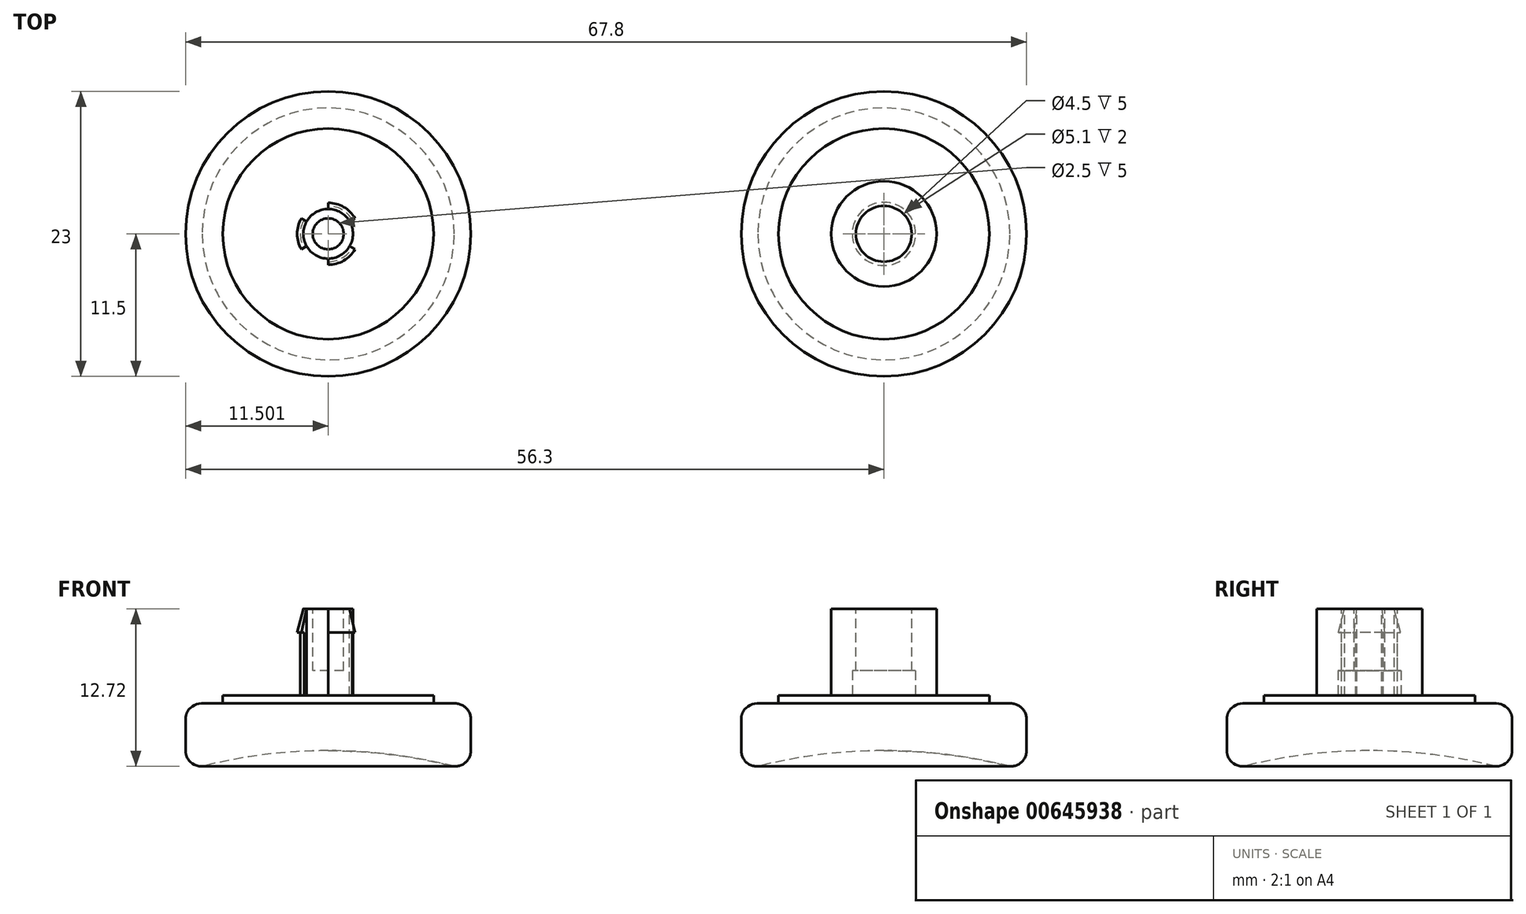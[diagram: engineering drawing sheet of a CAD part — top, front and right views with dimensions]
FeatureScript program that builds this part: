
annotation { "Feature Type Name" : "Feature", "Feature Type Description" : "" }
export const myFeature = defineFeature(function(context is Context, id is Id, definition is map)
    precondition{}
    {
        {
            var Q0;
            Q0=qCreatedBy(makeId("Top.planeOp"),FACE);
            var sketch = newSketch(context, id + "F0", { "sketchPlane" : qUnion([Q0])});
            skCircle(sketch, "E0", {"center": v(0, 0) * mm, "radius": 11.5 * mm});
            skCircle(sketch, "E1", {"center": v(0, 0) * mm, "radius": 4.25 * mm});
            skCircle(sketch, "E2", {"center": v(0, 0) * mm, "radius": 8.5 * mm});
            skSolve(sketch);
        }
        {
            var Q0;
            Q0=makeQuery(id+"F0.imprint","IMPRINT",FACE,{"disambiguationData":[TD([[makeQuery(id+"F0.imprint","IMPRINT",EDGE,{"derivedFrom":sQuery(id+"F0.wireOp",EDGE,"E0")}),1.0]])]});
            extrude(context, id + "F1", {"entities" : qUnion([Q0]), "depth" : 5.08 * mm, "offsetDistance" : 25.4 * mm});
        }
        {
            var Q0;
            Q0=makeQuery(id+"F0.imprint","IMPRINT",FACE,{"disambiguationData":[TD([[makeQuery(id+"F0.imprint","IMPRINT",EDGE,{"derivedFrom":sQuery(id+"F0.wireOp",EDGE,"E1")}),-1.0]])]});
            extrude(context, id + "F2", {"entities" : qUnion([Q0]), "operationType" : NewBodyOperationType.ADD, "depth" : 5.7 * mm, "offsetDistance" : 25.4 * mm});
        }
        {
            var Q0;
            Q0=makeQuery(id+"F0.imprint","IMPRINT",FACE,{"disambiguationData":[TD([[makeQuery(id+"F0.imprint","IMPRINT",EDGE,{"derivedFrom":sQuery(id+"F0.wireOp",EDGE,"E1")}),1.0]])]});
            extrude(context, id + "F3", {"entities" : qUnion([Q0]), "operationType" : NewBodyOperationType.ADD, "depth" : 7 * mm + 5.7 * mm, "offsetDistance" : 25.4 * mm});
        }
        {
            var Q0;
            Q0=makeQuery(id+"F1.opExtrude","CAP_EDGE",EDGE,{"disambiguationData":[OSD([sQuery(id+"F0.wireOp",EDGE,"E0")])],"isStart":false});
            var Q1;
            Q1=makeQuery(id+"F1.opExtrude","CAP_EDGE",EDGE,{"disambiguationData":[OSD([sQuery(id+"F0.wireOp",EDGE,"E0")])],"isStart":true});
            fillet(context, id + "F4", {"entities" : qUnion([Q0, Q1]), "radius" : 1.27 * mm, "tangentPropagation" : true, "allowEdgeOverflow" : false});
        }
        {
            var Q0;
            Q0=qCreatedBy(makeId("Top.planeOp"),FACE);
            var sketch = newSketch(context, id + "F5", { "sketchPlane" : qUnion([Q0])});
            skCircle(sketch, "E3", {"center": v(-44.8, 0) * mm, "radius": 11.5 * mm});
            skCircle(sketch, "E4", {"center": v(-44.8, 0) * mm, "radius": 8.5 * mm});
            skCircle(sketch, "E5", {"center": v(-44.8, 0) * mm, "radius": 2.5 * mm});
            skSolve(sketch);
        }
        {
            var Q0;
            Q0=makeQuery(id+"F5.imprint","IMPRINT",FACE,{"disambiguationData":[TD([[makeQuery(id+"F5.imprint","IMPRINT",EDGE,{"derivedFrom":sQuery(id+"F5.wireOp",EDGE,"E3")}),1.0]])]});
            extrude(context, id + "F6", {"entities" : qUnion([Q0]), "depth" : 5.08 * mm, "offsetDistance" : 25.4 * mm});
        }
        {
            var Q0;
            Q0=makeQuery(id+"F5.imprint","IMPRINT",FACE,{"disambiguationData":[TD([[makeQuery(id+"F5.imprint","IMPRINT",EDGE,{"derivedFrom":sQuery(id+"F5.wireOp",EDGE,"E4")}),1.0]])]});
            extrude(context, id + "F7", {"entities" : qUnion([Q0]), "operationType" : NewBodyOperationType.ADD, "depth" : 5.7 * mm, "offsetDistance" : 25.4 * mm});
        }
        {
            var Q0;
            Q0=makeQuery(id+"F5.imprint","IMPRINT",FACE,{"disambiguationData":[TD([[makeQuery(id+"F5.imprint","IMPRINT",EDGE,{"derivedFrom":sQuery(id+"F5.wireOp",EDGE,"E5")}),1.0]])]});
            extrude(context, id + "F8", {"entities" : qUnion([Q0]), "operationType" : NewBodyOperationType.ADD, "depth" : 7 * mm + 5.7 * mm, "offsetDistance" : 25.4 * mm});
        }
        {
            var Q0;
            Q0=makeQuery(id+"F3.opExtrude","CAP_FACE",FACE,{"disambiguationData":[OSD([sQuery(id+"F0.wireOp",EDGE,"E1")])],"isStart":false});
            var sketch = newSketch(context, id + "F9", { "sketchPlane" : qUnion([Q0])});
            skCircle(sketch, "E6", {"center": v(0, 0) * mm, "radius": 2.25 * mm});
            skSolve(sketch);
        }
        {
            var Q0;
            Q0=makeQuery(id+"F9.imprint","IMPRINT",FACE,{"disambiguationData":[TD([[makeQuery(id+"F9.imprint","IMPRINT",EDGE,{"derivedFrom":sQuery(id+"F9.wireOp",EDGE,"E6")}),1.0]])]});
            extrude(context, id + "F10", {"entities" : qUnion([Q0]), "operationType" : NewBodyOperationType.REMOVE, "oppositeDirection" : true, "depth" : 7 * mm});
        }
        {
            var Q0;
            Q0=makeQuery(id+"F6.opExtrude","CAP_EDGE",EDGE,{"disambiguationData":[OSD([sQuery(id+"F5.wireOp",EDGE,"E3")])],"isStart":false});
            var Q1;
            Q1=makeQuery(id+"F6.opExtrude","CAP_EDGE",EDGE,{"disambiguationData":[OSD([sQuery(id+"F5.wireOp",EDGE,"E3")])],"isStart":true});
            fillet(context, id + "F11", {"entities" : qUnion([Q0, Q1]), "radius" : 1.27 * mm, "tangentPropagation" : true, "allowEdgeOverflow" : false});
        }
        {
            var Q0;
            Q0=makeQuery(id+"F2.opExtrude","CAP_FACE",FACE,{"disambiguationData":[OSD([sQuery(id+"F0.wireOp",EDGE,"E1"),sQuery(id+"F0.wireOp",EDGE,"E2")])],"isStart":false});
            var sketch = newSketch(context, id + "F12", { "sketchPlane" : qUnion([Q0])});
            skCircle(sketch, "E7", {"center": v(0, 0) * mm, "radius": 2.55 * mm});
            skSolve(sketch);
        }
        {
            var Q0;
            Q0=qSketchRegion(id+"F12",true);
            extrude(context, id + "F13", {"entities" : qUnion([Q0]), "operationType" : NewBodyOperationType.REMOVE, "depth" : 2 * mm, "offsetDistance" : 25.4 * mm});
        }
        {
            var Q0;
            Q0=qCreatedBy(makeId("Front.planeOp"),FACE);
            var sketch = newSketch(context, id + "F14", { "sketchPlane" : qUnion([Q0])});
            skLineSegment(sketch, "E8", {"start": v(-44.8, 0) * mm, "end": v(-44.8, 12.71) * mm});
            skLineSegment(sketch, "E9", {"start": v(-44.8, 12.71) * mm, "end": v(-42.55, 12.71) * mm});
            skLineSegment(sketch, "E10", {"start": v(-42.55, 10.81) * mm, "end": v(-42.3, 10.81) * mm});
            skLineSegment(sketch, "E11", {"start": v(-42.55, 10.81) * mm, "end": v(-42.55, 5.71) * mm});
            skLineSegment(sketch, "E12", {"start": v(-42.55, 12.71) * mm, "end": v(-41.88, 12.8) * mm});
            skLineSegment(sketch, "E13", {"start": v(-42.55, 5.71) * mm, "end": v(-41.9, 5.71) * mm});
            skLineSegment(sketch, "E14", {"start": v(-42.3, 10.81) * mm, "end": v(-41.64, 10.81) * mm});
            skLineSegment(sketch, "E15", {"start": v(-41.64, 10.81) * mm, "end": v(-41.88, 12.8) * mm});
            skLineSegment(sketch, "E16", {"start": v(-41.9, 5.71) * mm, "end": v(-41.64, 10.81) * mm});
            skPoint(sketch, "E17", {"position": v(-42.8, 12.71) * mm});
            skLineSegment(sketch, "E18", {"start": v(-42.3, 10.81) * mm, "end": v(-42.8, 12.71) * mm});
            skLineSegment(sketch, "E19", {"start": v(-42.55, 5.71) * mm, "end": v(-44.8, 5.71) * mm});
            skLineSegment(sketch, "E20", {"start": v(-42.8, 12.71) * mm, "end": v(-42.8, 5.71) * mm});
            skLineSegment(sketch, "E21", {"start": v(-43.3, 12.71) * mm, "end": v(-43.3, 5.71) * mm});
            skSolve(sketch);
        }
        {
            var Q0;
            Q0=makeQuery(id+"F14.imprint","IMPRINT",FACE,{"disambiguationData":[TD([[makeQuery(id+"F14.imprint","IMPRINT",EDGE,{"derivedFrom":sQuery(id+"F14.wireOp",EDGE,"E10")}),-1.0]])]});
            var Q1;
            {var subQ0=sQuery(id+"F14.wireOp",EDGE,"E12");Q1=makeQuery(id+"F14.imprint","IMPRINT",FACE,{"disambiguationData":[TD([[makeQuery(id+"F14.imprint","IMPRINT",EDGE,{"derivedFrom":subQ0}),-1.0]])]});}
            var Q2;
            Q2=sQuery(id+"F14.wireOp",EDGE,"E8");
            revolve(context, id + "F15", {"operationType" : NewBodyOperationType.REMOVE, "entities" : qUnion([Q0, Q1]), "axis" : qUnion([Q2]), "revolveType" : RevolveType.FULL, "oppositeDirection" : true});
        }
        {
            var Q0;
            Q0=makeQuery(id+"F8.opExtrude","CAP_FACE",FACE,{"disambiguationData":[OSD([sQuery(id+"F5.wireOp",EDGE,"E5")])],"isStart":false});
            var sketch = newSketch(context, id + "F16", { "sketchPlane" : qUnion([Q0])});
            skCircle(sketch, "E22", {"center": v(-44.8, 0) * mm, "radius": 1.25 * mm});
            skSolve(sketch);
        }
        {
            var Q0;
            Q0=qSketchRegion(id+"F16",true);
            extrude(context, id + "F17", {"entities" : qUnion([Q0]), "operationType" : NewBodyOperationType.REMOVE, "oppositeDirection" : true, "depth" : 5 * mm, "offsetDistance" : 25.4 * mm});
        }
        {
            var Q0;
            Q0=makeQuery(id+"F8.opExtrude","CAP_FACE",FACE,{"disambiguationData":[OSD([sQuery(id+"F5.wireOp",EDGE,"E5")])],"isStart":false});
            var sketch = newSketch(context, id + "F18", { "sketchPlane" : qUnion([Q0])});
            skCircle(sketch, "E23", {"center": v(-44.8, 0) * mm, "radius": 3.54 * mm});
            skLineSegment(sketch, "E24", {"start": v(-44.8, 0) * mm, "end": v(-44.8, 3.54) * mm});
            skLineSegment(sketch, "E25", {"start": v(-44.8, 0) * mm, "end": v(-41.73, -1.77) * mm});
            skLineSegment(sketch, "E26", {"start": v(-44.8, 0) * mm, "end": v(-47.86, -1.77) * mm});
            skLineSegment(sketch, "E27", {"start": v(-44.8, 0) * mm, "end": v(-41.73, 1.77) * mm});
            skLineSegment(sketch, "E28", {"start": v(-44.8, 0) * mm, "end": v(-44.8, -3.54) * mm});
            skLineSegment(sketch, "E29", {"start": v(-44.8, 0) * mm, "end": v(-47.86, 1.77) * mm});
            skSolve(sketch);
        }
        {
            var Q0;
            {var subQ0=sQuery(id+"F18.wireOp",EDGE,"E24");var subQ1=sQuery(id+"F18.wireOp",EDGE,"E23");var subQ2=makeQuery(id+"F18.imprint","INTERSECT",VERTEX,{"derivedFrom":[subQ1,subQ0]});Q0=makeQuery(id+"F18.imprint","IMPRINT",FACE,{"disambiguationData":[TD([[makeQuery(id+"F18.imprint","IMPRINT",EDGE,{"disambiguationData":[TD([[subQ2,-1.0]])],"derivedFrom":subQ1}),1.0]])]});}
            var Q1;
            {var subQ0=sQuery(id+"F18.wireOp",EDGE,"E25");var subQ1=sQuery(id+"F18.wireOp",EDGE,"E23");var subQ2=makeQuery(id+"F18.imprint","INTERSECT",VERTEX,{"derivedFrom":[subQ1,subQ0]});Q1=makeQuery(id+"F18.imprint","IMPRINT",FACE,{"disambiguationData":[TD([[makeQuery(id+"F18.imprint","IMPRINT",EDGE,{"disambiguationData":[TD([[subQ2,-1.0]])],"derivedFrom":subQ1}),1.0]])]});}
            var Q2;
            {var subQ0=sQuery(id+"F18.wireOp",EDGE,"E26");var subQ1=sQuery(id+"F18.wireOp",EDGE,"E23");var subQ2=makeQuery(id+"F18.imprint","INTERSECT",VERTEX,{"derivedFrom":[subQ1,subQ0]});Q2=makeQuery(id+"F18.imprint","IMPRINT",FACE,{"disambiguationData":[TD([[makeQuery(id+"F18.imprint","IMPRINT",EDGE,{"disambiguationData":[TD([[subQ2,-1.0]])],"derivedFrom":subQ1}),1.0]])]});}
            var Q3;
            {var subQ0=sQuery(id+"F18.wireOp",EDGE,"E25");var subQ1=makeQuery(id+"F17.boolean.opBoolean","COPY",EDGE,{"derivedFrom":makeQuery(id+"F17.opExtrude","CAP_EDGE",EDGE,{"disambiguationData":[OSD([sQuery(id+"F16.wireOp",EDGE,"E22")])],"isStart":true})});var subQ2=makeQuery(id+"F18.imprint","INTERSECT",VERTEX,{"derivedFrom":[subQ1,subQ0]});Q3=makeQuery(id+"F18.imprint","IMPRINT",FACE,{"disambiguationData":[TD([[makeQuery(id+"F18.imprint","IMPRINT",EDGE,{"disambiguationData":[TD([[subQ2,-1.0]])],"derivedFrom":subQ1}),-1.0]])]});}
            var Q4;
            {var subQ0=sQuery(id+"F18.wireOp",EDGE,"E26");var subQ1=makeQuery(id+"F17.boolean.opBoolean","COPY",EDGE,{"derivedFrom":makeQuery(id+"F17.opExtrude","CAP_EDGE",EDGE,{"disambiguationData":[OSD([sQuery(id+"F16.wireOp",EDGE,"E22")])],"isStart":true})});var subQ2=makeQuery(id+"F18.imprint","INTERSECT",VERTEX,{"derivedFrom":[subQ1,subQ0]});Q4=makeQuery(id+"F18.imprint","IMPRINT",FACE,{"disambiguationData":[TD([[makeQuery(id+"F18.imprint","IMPRINT",EDGE,{"disambiguationData":[TD([[subQ2,-1.0]])],"derivedFrom":subQ1}),-1.0]])]});}
            var Q5;
            {var subQ0=sQuery(id+"F18.wireOp",EDGE,"E24");var subQ1=makeQuery(id+"F17.boolean.opBoolean","COPY",EDGE,{"derivedFrom":makeQuery(id+"F17.opExtrude","CAP_EDGE",EDGE,{"disambiguationData":[OSD([sQuery(id+"F16.wireOp",EDGE,"E22")])],"isStart":true})});var subQ2=makeQuery(id+"F18.imprint","INTERSECT",VERTEX,{"derivedFrom":[subQ1,subQ0]});Q5=makeQuery(id+"F18.imprint","IMPRINT",FACE,{"disambiguationData":[TD([[makeQuery(id+"F18.imprint","IMPRINT",EDGE,{"disambiguationData":[TD([[subQ2,-1.0]])],"derivedFrom":subQ1}),-1.0]])]});}
            extrude(context, id + "F19", {"entities" : qUnion([Q0, Q1, Q2, Q3, Q4, Q5]), "operationType" : NewBodyOperationType.REMOVE, "oppositeDirection" : true, "depth" : 7 * mm, "offsetDistance" : 25.4 * mm});
        }
        {
            var Q0;
            Q0=qCreatedBy(makeId("Front.planeOp"),FACE);
            var sketch = newSketch(context, id + "F20", { "sketchPlane" : qUnion([Q0])});
            skLineSegment(sketch, "E30", {"start": v(0, 0) * mm, "end": v(0, 1.27) * mm});
            skLineSegment(sketch, "E31", {"start": v(0, 0) * mm, "end": v(10.16, 0) * mm});
            skArc(sketch, "E32", {"start": v(10.16, 0) * mm, "mid": v(5.12, 0.95) * mm, "end": v(0, 1.27) * mm});
            skLineSegment(sketch, "E33", {"start": v(0, 0) * mm, "end": v(0, -2.72) * mm});
            skSolve(sketch);
        }
        {
            var Q0;
            Q0 = qSketchRegion(id + "F20", true);
            var Q1;
            Q1=sQuery(id+"F20.wireOp",EDGE,"E33");
            revolve(context, id + "F21", {"operationType" : NewBodyOperationType.REMOVE, "entities" : qUnion([Q0]), "axis" : qUnion([Q1]), "revolveType" : RevolveType.FULL, "oppositeDirection" : true});
        }
        {
            var Q0;
            Q0=qCreatedBy(makeId("Front.planeOp"),FACE);
            var sketch = newSketch(context, id + "F22", { "sketchPlane" : qUnion([Q0])});
            skPoint(sketch, "E34", {"position": v(-44.8, 0) * mm});
            skLineSegment(sketch, "E35", {"start": v(-44.8, 0) * mm, "end": v(-34.64, 0) * mm});
            skLineSegment(sketch, "E36", {"start": v(-44.8, 0) * mm, "end": v(-44.8, 1.27) * mm});
            skArc(sketch, "E37", {"start": v(-34.64, 0) * mm, "mid": v(-39.68, 0.95) * mm, "end": v(-44.8, 1.27) * mm});
            skSolve(sketch);
        }
        {
            var Q0;
            Q0 = qSketchRegion(id + "F22", true);
            var Q1;
            Q1=sQuery(id+"F22.wireOp",EDGE,"E36");
            revolve(context, id + "F23", {"operationType" : NewBodyOperationType.REMOVE, "entities" : qUnion([Q0]), "axis" : qUnion([Q1]), "revolveType" : RevolveType.FULL});
        }
    });
